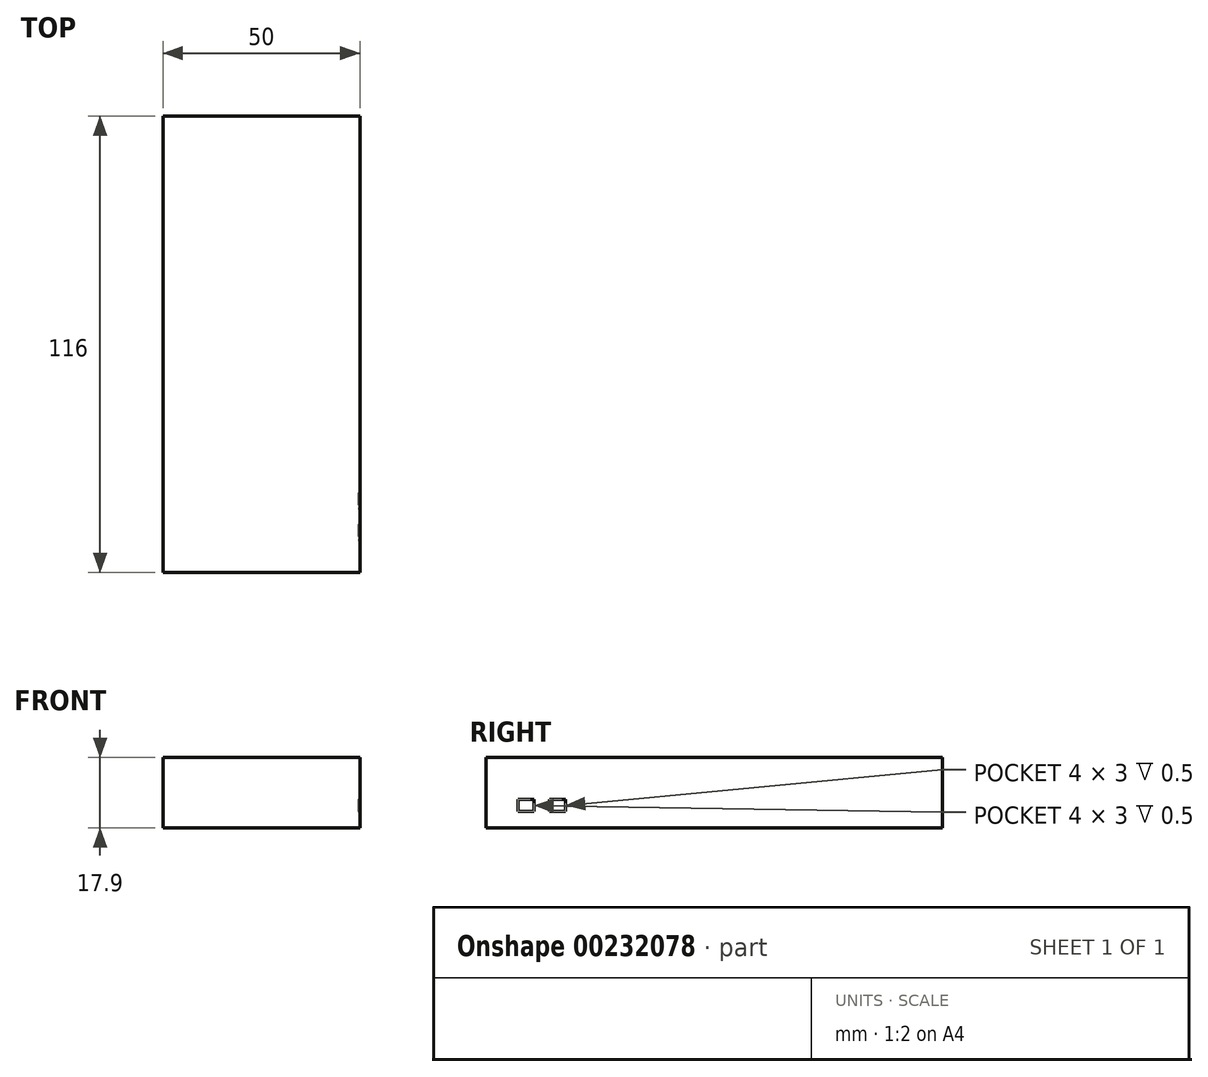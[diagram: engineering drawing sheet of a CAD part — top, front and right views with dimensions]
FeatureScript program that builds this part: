
annotation { "Feature Type Name" : "Feature", "Feature Type Description" : "" }
export const myFeature = defineFeature(function(context is Context, id is Id, definition is map)
    precondition{}
    {
        {
            assignVariable(context, id + "F0", {"name" : "D", "anyValue" : 17.9});
        }
        {
            var Q0;
            Q0=qCreatedBy(makeId("Top.planeOp"),FACE);
            var sketch = newSketch(context, id + "F1", { "sketchPlane" : qUnion([Q0])});
            skLineSegment(sketch, "E0.bottom", {"start": v(25, 58) * mm, "end": v(-25, 58) * mm});
            skLineSegment(sketch, "E0.top", {"start": v(25, -58) * mm, "end": v(-25, -58) * mm});
            skLineSegment(sketch, "E0.left", {"start": v(25, 58) * mm, "end": v(25, -58) * mm});
            skLineSegment(sketch, "E0.right", {"start": v(-25, 58) * mm, "end": v(-25, -58) * mm});
            skPoint(sketch, "E0.middle", {"position": v(0, 0) * mm});
            skSolve(sketch);
        }
        {
            var Q0;
            Q0 = qSketchRegion(id + "F1", true);
            extrude(context, id + "F2", {"entities" : qUnion([Q0]), "depth" : (getVariable(context, 'D')) * mm});
        }
        {
            var Q0;
            Q0=makeQuery(id+"F2.opExtrude","SWEPT_FACE",FACE,{"disambiguationData":[OSD([sQuery(id+"F1.wireOp",EDGE,"E0.left")])]});
            var sketch = newSketch(context, id + "F3", { "sketchPlane" : qUnion([Q0])});
            skLineSegment(sketch, "E1.bottom", {"start": v(-45.79, 7.2) * mm, "end": v(-49.79, 7.2) * mm});
            skLineSegment(sketch, "E1.top", {"start": v(-45.79, 4.2) * mm, "end": v(-49.79, 4.2) * mm});
            skLineSegment(sketch, "E1.left", {"start": v(-45.79, 7.2) * mm, "end": v(-45.79, 4.2) * mm});
            skLineSegment(sketch, "E1.right", {"start": v(-49.79, 7.2) * mm, "end": v(-49.79, 4.2) * mm});
            skPoint(sketch, "E1.middle", {"position": v(-47.79, 5.7) * mm});
            skPoint(sketch, "E2.1.0.0", {"position": v(-39.79, 5.7) * mm});
            skLineSegment(sketch, "E2.1.0.1", {"start": v(-37.79, 7.2) * mm, "end": v(-41.79, 7.2) * mm});
            skLineSegment(sketch, "E2.1.0.2", {"start": v(-37.79, 4.2) * mm, "end": v(-41.79, 4.2) * mm});
            skLineSegment(sketch, "E2.1.0.3", {"start": v(-37.79, 7.2) * mm, "end": v(-37.79, 4.2) * mm});
            skLineSegment(sketch, "E2.1.0.4", {"start": v(-41.79, 7.2) * mm, "end": v(-41.79, 4.2) * mm});
            skLineSegment(sketch, "E2.direction1", {"start": v(-49.79, 4.2) * mm, "end": v(-41.79, 4.2) * mm, "construction": true});
            skSolve(sketch);
        }
        {
            var Q0;
            Q0 = qSketchRegion(id + "F3", true);
            extrude(context, id + "F4", {"entities" : qUnion([Q0]), "operationType" : NewBodyOperationType.REMOVE, "oppositeDirection" : true, "depth" : .5 * mm});
        }
    });
